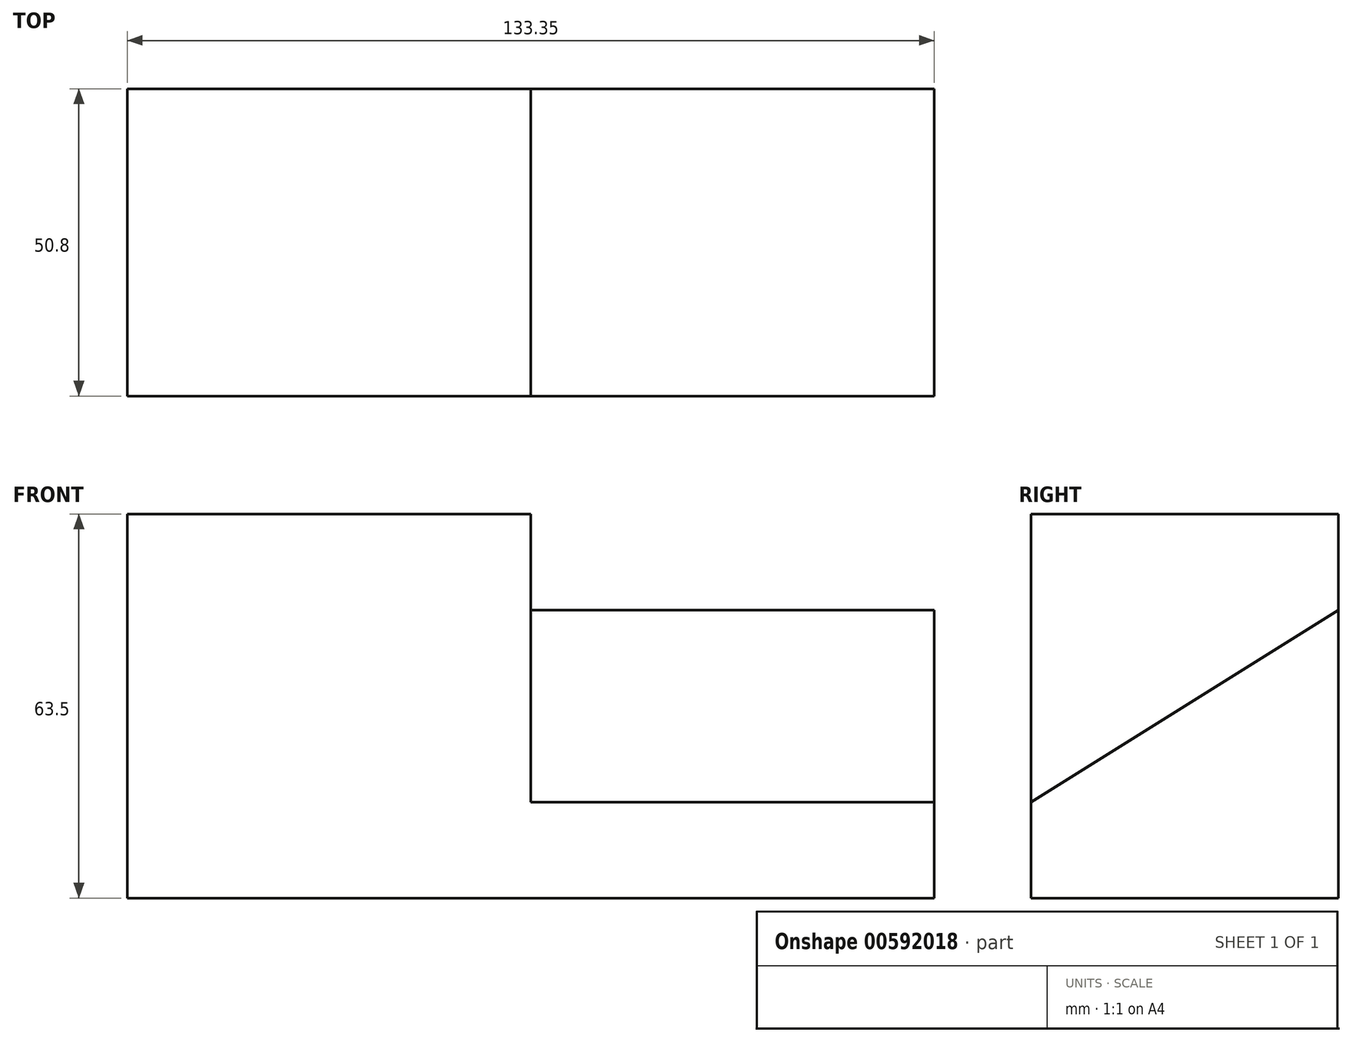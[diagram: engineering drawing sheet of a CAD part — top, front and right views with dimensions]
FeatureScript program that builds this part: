
annotation { "Feature Type Name" : "Feature", "Feature Type Description" : "" }
export const myFeature = defineFeature(function(context is Context, id is Id, definition is map)
    precondition{}
    {
        {
            var Q0;
            Q0=qCreatedBy(makeId("Front.planeOp"),FACE);
            var sketch = newSketch(context, id + "F0", { "sketchPlane" : qUnion([Q0])});
            skLineSegment(sketch, "E0", {"start": v(0, 0) * mm, "end": v(66.67, 0) * mm});
            skLineSegment(sketch, "E1", {"start": v(0, 0) * mm, "end": v(0, 63.5) * mm});
            skLineSegment(sketch, "E2", {"start": v(0, 63.5) * mm, "end": v(66.68, 63.5) * mm});
            skLineSegment(sketch, "E3", {"start": v(66.68, 63.5) * mm, "end": v(66.68, 0) * mm});
            skSolve(sketch);
        }
        {
            var Q0;
            Q0=makeQuery(id+"F0.imprint","IMPRINT",FACE,{"disambiguationData":[TD([[makeQuery(id+"F0.imprint","IMPRINT",EDGE,{"derivedFrom":sQuery(id+"F0.wireOp",EDGE,"E0")}),1.0]])]});
            extrude(context, id + "F1", {"entities" : qUnion([Q0]), "depth" : 50.8 * mm, "offsetDistance" : 25.4 * mm});
        }
        {
            var Q0;
            Q0=makeQuery(id+"F1.opExtrude","SWEPT_FACE",FACE,{"disambiguationData":[OSD([sQuery(id+"F0.wireOp",EDGE,"E3")])]});
            var sketch = newSketch(context, id + "F2", { "sketchPlane" : qUnion([Q0])});
            skLineSegment(sketch, "E4", {"start": v(-50.8, 0) * mm, "end": v(-50.8, 15.88) * mm});
            skLineSegment(sketch, "E5", {"start": v(-50.8, 15.88) * mm, "end": v(0, 47.62) * mm});
            skLineSegment(sketch, "E6", {"start": v(0, 47.62) * mm, "end": v(0, 0) * mm});
            skLineSegment(sketch, "E7", {"start": v(0, 0) * mm, "end": v(-50.8, 0) * mm});
            skSolve(sketch);
        }
        {
            var Q0;
            Q0=makeQuery(id+"F2.imprint","IMPRINT",FACE,{"disambiguationData":[TD([[makeQuery(id+"F2.imprint","IMPRINT",EDGE,{"derivedFrom":sQuery(id+"F2.wireOp",EDGE,"E4")}),1.0]])]});
            extrude(context, id + "F3", {"entities" : qUnion([Q0]), "operationType" : NewBodyOperationType.ADD, "depth" : 66.67 * mm, "offsetDistance" : 25.4 * mm});
        }
    });
